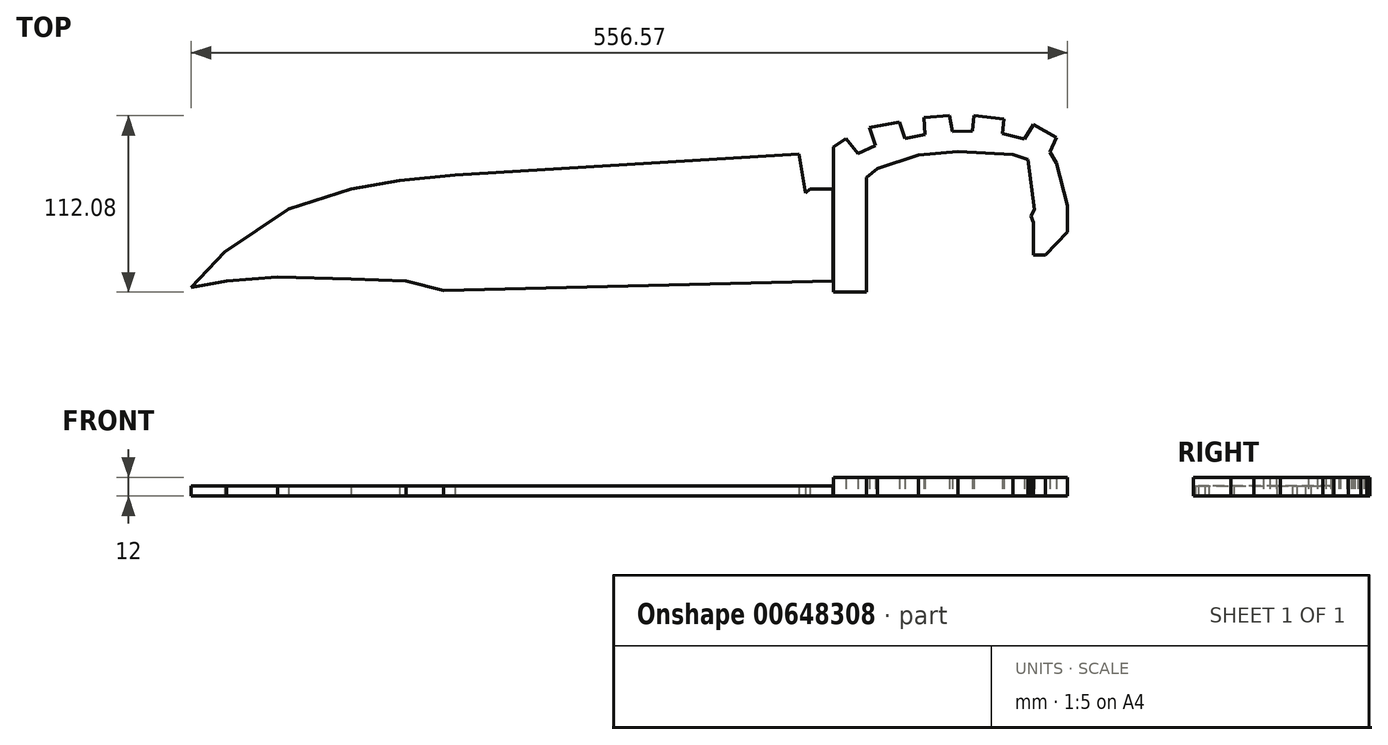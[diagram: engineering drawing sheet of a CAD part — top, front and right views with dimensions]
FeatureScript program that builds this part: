
annotation { "Feature Type Name" : "Feature", "Feature Type Description" : "" }
export const myFeature = defineFeature(function(context is Context, id is Id, definition is map)
    precondition{}
    {
        {
            var Q0;
            Q0=qCreatedBy(makeId("Top.planeOp"),FACE);
            var sketch = newSketch(context, id + "F0", { "sketchPlane" : qUnion([Q0])});
            skLineSegment(sketch, "E0", {"start": v(0, 22.64) * mm, "end": v(21.03, 45.2) * mm});
            skLineSegment(sketch, "E1", {"start": v(21.03, 45.2) * mm, "end": v(61.76, 72.46) * mm});
            skLineSegment(sketch, "E2", {"start": v(61.76, 72.46) * mm, "end": v(101.55, 85.3) * mm});
            skLineSegment(sketch, "E3", {"start": v(101.55, 85.3) * mm, "end": v(132.25, 90.63) * mm});
            skLineSegment(sketch, "E4", {"start": v(132.25, 90.63) * mm, "end": v(167.34, 94.07) * mm});
            skLineSegment(sketch, "E5", {"start": v(167.34, 94.07) * mm, "end": v(386.02, 107.55) * mm});
            skLineSegment(sketch, "E6", {"start": v(386.02, 107.55) * mm, "end": v(390.1, 82.48) * mm});
            skLineSegment(sketch, "E7", {"start": v(390.1, 82.48) * mm, "end": v(392.92, 85.3) * mm});
            skLineSegment(sketch, "E8", {"start": v(392.92, 85.3) * mm, "end": v(407.64, 85.3) * mm});
            skLineSegment(sketch, "E9", {"start": v(407.64, 85.3) * mm, "end": v(407.64, 26.72) * mm});
            skLineSegment(sketch, "E10", {"start": v(407.64, 26.72) * mm, "end": v(160.14, 20.76) * mm});
            skLineSegment(sketch, "E11", {"start": v(160.14, 20.76) * mm, "end": v(136.33, 26.72) * mm});
            skLineSegment(sketch, "E12", {"start": v(136.33, 26.72) * mm, "end": v(101.55, 27.97) * mm});
            skLineSegment(sketch, "E13", {"start": v(101.55, 27.97) * mm, "end": v(54.87, 29.22) * mm});
            skLineSegment(sketch, "E14", {"start": v(54.87, 29.22) * mm, "end": v(22.29, 26.72) * mm});
            skLineSegment(sketch, "E15", {"start": v(22.29, 26.72) * mm, "end": v(0, 22.64) * mm});
            skSolve(sketch);
        }
        {
            var Q0;
            Q0 = qSketchRegion(id + "F0", true);
            extrude(context, id + "F1", {"entities" : qUnion([Q0]), "depth" : 6.35 * mm, "offsetDistance" : 25 * mm});
        }
        {
            var Q0;
            Q0=qCreatedBy(makeId("Top.planeOp"),FACE);
            var sketch = newSketch(context, id + "F2", { "sketchPlane" : qUnion([Q0])});
            skLineSegment(sketch, "E16", {"start": v(407.72, 26.62) * mm, "end": v(407.72, 19.62) * mm});
            skLineSegment(sketch, "E17", {"start": v(407.72, 19.62) * mm, "end": v(428.93, 19.62) * mm});
            skLineSegment(sketch, "E18", {"start": v(428.93, 19.62) * mm, "end": v(428.93, 92.5) * mm});
            skLineSegment(sketch, "E19", {"start": v(428.93, 92.5) * mm, "end": v(435.67, 98.24) * mm});
            skLineSegment(sketch, "E20", {"start": v(435.67, 98.24) * mm, "end": v(461.83, 106.76) * mm});
            skLineSegment(sketch, "E21", {"start": v(461.83, 106.76) * mm, "end": v(486.8, 108.94) * mm});
            skLineSegment(sketch, "E22", {"start": v(486.8, 108.94) * mm, "end": v(521.89, 106.96) * mm});
            skLineSegment(sketch, "E23", {"start": v(521.89, 106.96) * mm, "end": v(531.4, 103.79) * mm});
            skLineSegment(sketch, "E24", {"start": v(531.4, 103.79) * mm, "end": v(535.56, 72.27) * mm});
            skLineSegment(sketch, "E25", {"start": v(535.56, 72.27) * mm, "end": v(533.38, 68.11) * mm});
            skLineSegment(sketch, "E26", {"start": v(533.38, 68.11) * mm, "end": v(534.97, 63.95) * mm});
            skLineSegment(sketch, "E27", {"start": v(534.97, 63.95) * mm, "end": v(534.97, 43.14) * mm});
            skLineSegment(sketch, "E28", {"start": v(534.97, 43.14) * mm, "end": v(542.5, 43.14) * mm});
            skLineSegment(sketch, "E29", {"start": v(542.5, 43.14) * mm, "end": v(556.57, 57.8) * mm});
            skLineSegment(sketch, "E30", {"start": v(556.57, 57.8) * mm, "end": v(556.57, 74.85) * mm});
            skLineSegment(sketch, "E31", {"start": v(556.57, 74.85) * mm, "end": v(549.44, 101.6) * mm});
            skLineSegment(sketch, "E32", {"start": v(549.44, 101.6) * mm, "end": v(545.47, 108.55) * mm});
            skLineSegment(sketch, "E33", {"start": v(545.47, 108.55) * mm, "end": v(549.44, 117.86) * mm});
            skLineSegment(sketch, "E34", {"start": v(549.44, 117.86) * mm, "end": v(534.97, 125.99) * mm});
            skLineSegment(sketch, "E35", {"start": v(534.97, 125.99) * mm, "end": v(529.08, 117.02) * mm});
            skLineSegment(sketch, "E36", {"start": v(529.08, 117.02) * mm, "end": v(515.08, 120.43) * mm});
            skLineSegment(sketch, "E37", {"start": v(515.08, 120.43) * mm, "end": v(516.02, 129.79) * mm});
            skLineSegment(sketch, "E38", {"start": v(516.02, 129.79) * mm, "end": v(496.98, 131.7) * mm});
            skLineSegment(sketch, "E39", {"start": v(496.98, 131.7) * mm, "end": v(496, 121.97) * mm});
            skLineSegment(sketch, "E40", {"start": v(483.37, 121.77) * mm, "end": v(481.49, 131.7) * mm});
            skLineSegment(sketch, "E41", {"start": v(481.49, 131.7) * mm, "end": v(465.34, 130.61) * mm});
            skLineSegment(sketch, "E42", {"start": v(465.34, 130.61) * mm, "end": v(466.07, 119.82) * mm});
            skLineSegment(sketch, "E43", {"start": v(466.07, 119.82) * mm, "end": v(453.32, 117.4) * mm});
            skLineSegment(sketch, "E44", {"start": v(453.32, 117.4) * mm, "end": v(449.67, 127.66) * mm});
            skLineSegment(sketch, "E45", {"start": v(449.67, 127.66) * mm, "end": v(430.8, 124.08) * mm});
            skLineSegment(sketch, "E46", {"start": v(430.8, 124.08) * mm, "end": v(434.46, 112.93) * mm});
            skLineSegment(sketch, "E47", {"start": v(434.46, 112.93) * mm, "end": v(423.27, 107.86) * mm});
            skLineSegment(sketch, "E48", {"start": v(423.27, 107.86) * mm, "end": v(415.6, 117.4) * mm});
            skLineSegment(sketch, "E49", {"start": v(407.72, 26.62) * mm, "end": v(407.72, 111.83) * mm});
            skLineSegment(sketch, "E50", {"start": v(415.6, 117.4) * mm, "end": v(407.72, 111.83) * mm});
            skLineSegment(sketch, "E51", {"start": v(496, 121.97) * mm, "end": v(483.37, 121.77) * mm});
            skSolve(sketch);
        }
        {
            var Q0;
            Q0 = qSketchRegion(id + "F2", true);
            extrude(context, id + "F3", {"entities" : qUnion([Q0]), "depth" : 12 * mm, "offsetDistance" : 25 * mm});
        }
    });
